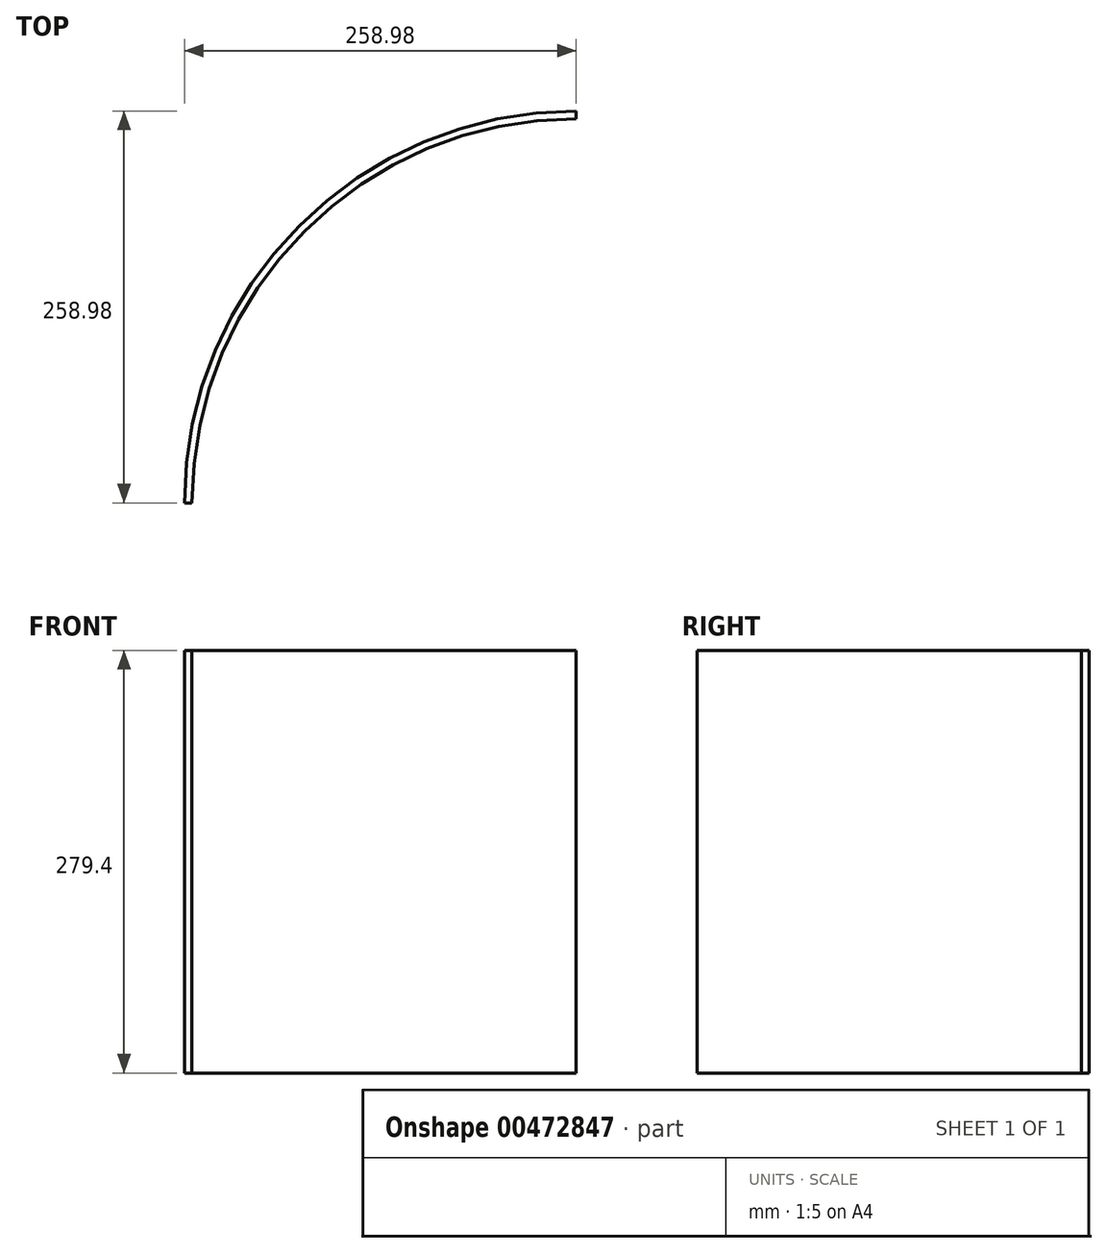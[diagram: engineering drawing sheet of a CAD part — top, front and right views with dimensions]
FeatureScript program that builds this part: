
annotation { "Feature Type Name" : "Feature", "Feature Type Description" : "" }
export const myFeature = defineFeature(function(context is Context, id is Id, definition is map)
    precondition{}
    {
        {
            var Q0;
            Q0=qCreatedBy(makeId("Top.planeOp"),FACE);
            var sketch = newSketch(context, id + "F0", { "sketchPlane" : qUnion([Q0])});
            skArc(sketch, "E0", {"start": v(-254, 0) * mm, "mid": v(-179.6, 179.6) * mm, "end": v(0, 254) * mm});
            skArc(sketch, "E1.0", {"start": v(-258.98, 0) * mm, "mid": v(-183.13, 183.13) * mm, "end": v(0, 258.98) * mm});
            skLineSegment(sketch, "E2", {"start": v(0, 258.98) * mm, "end": v(0, 254) * mm});
            skLineSegment(sketch, "E3", {"start": v(-258.98, 0) * mm, "end": v(-254, 0) * mm});
            skSolve(sketch);
        }
        {
            var Q0;
            Q0 = qSketchRegion(id + "F0", true);
            extrude(context, id + "F1", {"entities" : qUnion([Q0]), "depth" : 279.4 * mm});
        }
    });
